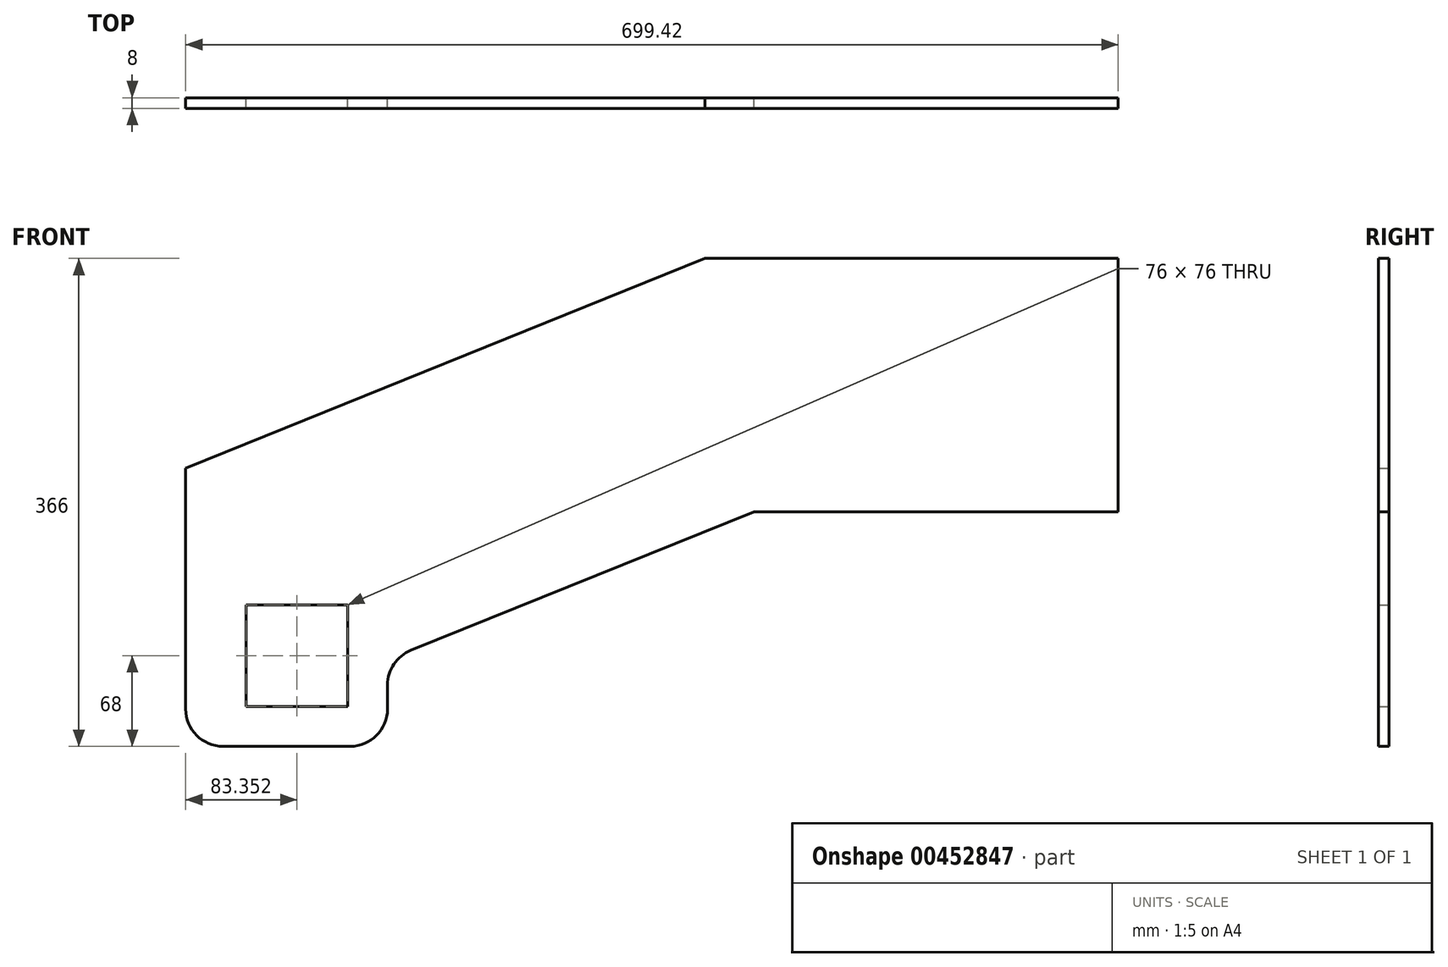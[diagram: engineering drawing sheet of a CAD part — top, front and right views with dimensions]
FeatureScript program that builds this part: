
annotation { "Feature Type Name" : "Feature", "Feature Type Description" : "" }
export const myFeature = defineFeature(function(context is Context, id is Id, definition is map)
    precondition{}
    {
        {
            var Q0;
            Q0=qCreatedBy(makeId("Front.planeOp"),FACE);
            var sketch = newSketch(context, id + "F0", { "sketchPlane" : qUnion([Q0])});
            skLineSegment(sketch, "E0", {"start": v(0, 0) * mm, "end": v(0, -190) * mm});
            skLineSegment(sketch, "E1", {"start": v(0, -190) * mm, "end": v(-273.07, -190) * mm});
            skLineSegment(sketch, "E2", {"start": v(-576.07, -366) * mm, "end": v(-671.42, -366) * mm});
            skLineSegment(sketch, "E3", {"start": v(-699.42, -338) * mm, "end": v(-699.42, -157.33) * mm});
            skLineSegment(sketch, "E4", {"start": v(-699.42, -157.33) * mm, "end": v(-310, 0) * mm});
            skLineSegment(sketch, "E5", {"start": v(-310, 0) * mm, "end": v(0, 0) * mm});
            skLineSegment(sketch, "E6", {"start": v(-310, 0) * mm, "end": v(-236.14, -380) * mm, "construction": true});
            skLineSegment(sketch, "E7.bottom", {"start": v(-654.07, -260) * mm, "end": v(-578.07, -260) * mm});
            skLineSegment(sketch, "E7.top", {"start": v(-654.07, -336) * mm, "end": v(-578.07, -336) * mm});
            skLineSegment(sketch, "E7.left", {"start": v(-654.07, -260) * mm, "end": v(-654.07, -336) * mm});
            skLineSegment(sketch, "E7.right", {"start": v(-578.07, -260) * mm, "end": v(-578.07, -336) * mm});
            skLineSegment(sketch, "E8", {"start": v(-548.07, -338) * mm, "end": v(-548.07, -320) * mm});
            skLineSegment(sketch, "E9", {"start": v(-530.56, -294.03) * mm, "end": v(-273.07, -190) * mm});
            skPoint(sketch, "E10.visualSharp", {"position": v(-548.07, -301.1) * mm});
            skArc(sketch, "E10.filletArc", {"start": v(-530.56, -294.03) * mm, "mid": v(-543.28, -304.34) * mm, "end": v(-548.07, -320) * mm});
            skPoint(sketch, "E11.visualSharp", {"position": v(-548.07, -366) * mm});
            skArc(sketch, "E11.filletArc", {"start": v(-576.07, -366) * mm, "mid": v(-556.27, -357.8) * mm, "end": v(-548.07, -338) * mm});
            skPoint(sketch, "E12.visualSharp", {"position": v(-699.42, -366) * mm});
            skArc(sketch, "E12.filletArc", {"start": v(-699.42, -338) * mm, "mid": v(-691.22, -357.8) * mm, "end": v(-671.42, -366) * mm});
            skSolve(sketch);
        }
        {
            var Q0;
            Q0=makeQuery(id+"F0.imprint","IMPRINT",FACE,{"disambiguationData":[TD([[makeQuery(id+"F0.imprint","IMPRINT",EDGE,{"derivedFrom":sQuery(id+"F0.wireOp",EDGE,"E0")}),-1.0]])]});
            extrude(context, id + "F1", {"entities" : qUnion([Q0]), "depth" : 8 * mm});
        }
    });
